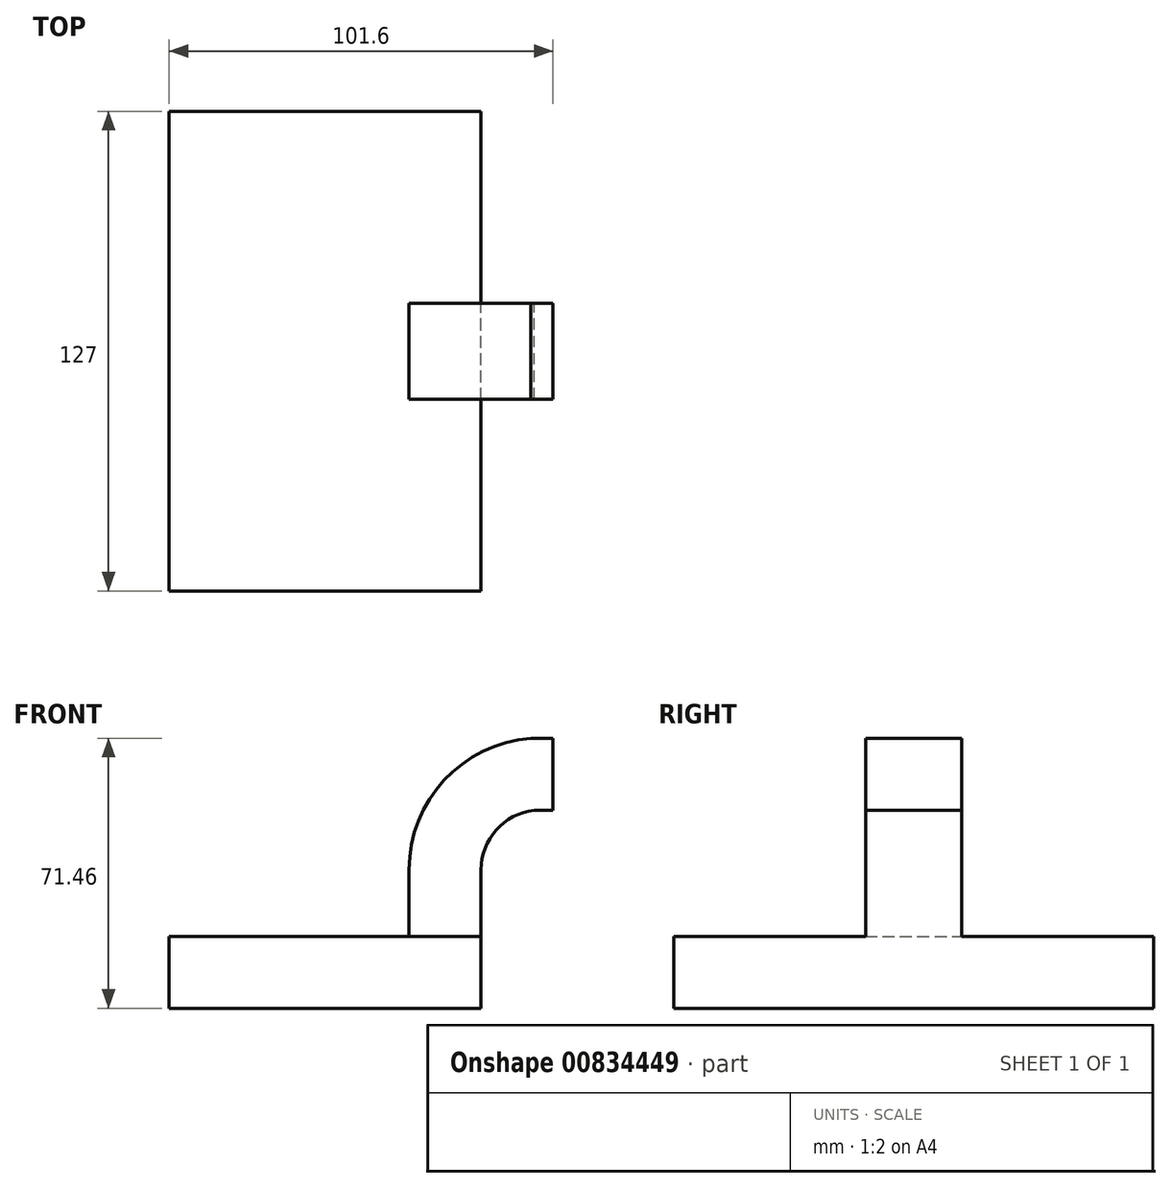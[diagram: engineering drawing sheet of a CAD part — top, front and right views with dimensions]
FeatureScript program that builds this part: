
annotation { "Feature Type Name" : "Feature", "Feature Type Description" : "" }
export const myFeature = defineFeature(function(context is Context, id is Id, definition is map)
    precondition{}
    {
        {
            var Q0;
            Q0=qCreatedBy(makeId("Front.planeOp"),FACE);
            var sketch = newSketch(context, id + "F0", { "sketchPlane" : qUnion([Q0])});
            skLineSegment(sketch, "E0.bottom", {"start": v(-41.28, 9.53) * mm, "end": v(41.28, 9.53) * mm});
            skLineSegment(sketch, "E0.top", {"start": v(-41.28, -9.53) * mm, "end": v(41.28, -9.53) * mm});
            skLineSegment(sketch, "E0.left", {"start": v(-41.28, 9.53) * mm, "end": v(-41.28, -9.53) * mm});
            skLineSegment(sketch, "E0.right", {"start": v(41.28, 9.53) * mm, "end": v(41.28, -9.53) * mm});
            skPoint(sketch, "E0.middle", {"position": v(0, 0) * mm});
            skLineSegment(sketch, "E1.bottom", {"start": v(111.12, 38.1) * mm, "end": v(60.32, 38.1) * mm});
            skLineSegment(sketch, "E1.top", {"start": v(111.12, 66.67) * mm, "end": v(60.32, 66.67) * mm});
            skLineSegment(sketch, "E1.left", {"start": v(111.13, 38.1) * mm, "end": v(111.13, 66.68) * mm});
            skLineSegment(sketch, "E1.right", {"start": v(60.32, 38.1) * mm, "end": v(60.32, 66.68) * mm});
            skPoint(sketch, "E1.middle", {"position": v(85.72, 52.39) * mm});
            skLineSegment(sketch, "E2", {"start": v(60.32, 42.88) * mm, "end": v(72.29, 42.88) * mm});
            skLineSegment(sketch, "E3", {"start": v(60.32, 42.88) * mm, "end": v(88.7, 42.88) * mm});
            skLineSegment(sketch, "E4", {"start": v(60.32, 42.88) * mm, "end": v(55.34, 42.88) * mm});
            skLineSegment(sketch, "E5", {"start": v(41.28, 9.53) * mm, "end": v(41.28, 27.1) * mm});
            skArc(sketch, "E6", {"start": v(41.28, 27.1) * mm, "mid": v(45.3, 37.67) * mm, "end": v(55.34, 42.88) * mm});
            skLineSegment(sketch, "E7.0", {"start": v(60.32, 61.93) * mm, "end": v(54.47, 61.93) * mm});
            skArc(sketch, "E7.1", {"start": v(22.23, 27.1) * mm, "mid": v(31.52, 50.83) * mm, "end": v(54.47, 61.93) * mm});
            skLineSegment(sketch, "E7.2", {"start": v(22.23, 9.53) * mm, "end": v(22.23, 27.1) * mm});
            skLineSegment(sketch, "E8", {"start": v(72.29, 61.93) * mm, "end": v(60.32, 61.93) * mm});
            skLineSegment(sketch, "E9", {"start": v(85.72, 52.39) * mm, "end": v(85.72, 61.93) * mm});
            skLineSegment(sketch, "E10", {"start": v(85.72, 61.93) * mm, "end": v(72.29, 61.93) * mm});
            skLineSegment(sketch, "E11", {"start": v(85.72, 52.39) * mm, "end": v(85.72, 42.88) * mm});
            skFitSpline(sketch, "E12", {"points": [v(-41.28, 9.53) * mm, v(54.47, 61.93) * mm], "startDerivative": vector(47.6, 104.25) * mm, "endDerivative": vector(176.97, 4.31) * mm});
            skSolve(sketch);
        }
        {
            var Q0;
            {var subQ0=sQuery(id+"F0.wireOp",EDGE,"E4");Q0=makeQuery(id+"F0.imprint","IMPRINT",FACE,{"disambiguationData":[TD([[makeQuery(id+"F0.imprint","IMPRINT",EDGE,{"derivedFrom":subQ0}),-1.0]])]});}
            extrude(context, id + "F1", {"entities" : qUnion([Q0]), "endBound" : BoundingType.SYMMETRIC, "depth" : 25.4 * mm, "offsetDistance" : 25.4 * mm});
        }
        {
            var Q0;
            Q0=makeQuery(id+"F0.imprint","IMPRINT",FACE,{"disambiguationData":[TD([[makeQuery(id+"F0.imprint","IMPRINT",EDGE,{"derivedFrom":sQuery(id+"F0.wireOp",EDGE,"E0.top")}),1.0]])]});
            extrude(context, id + "F2", {"entities" : qUnion([Q0]), "operationType" : NewBodyOperationType.ADD, "endBound" : BoundingType.SYMMETRIC, "depth" : 127 * mm, "offsetDistance" : 25.4 * mm});
        }
    });
